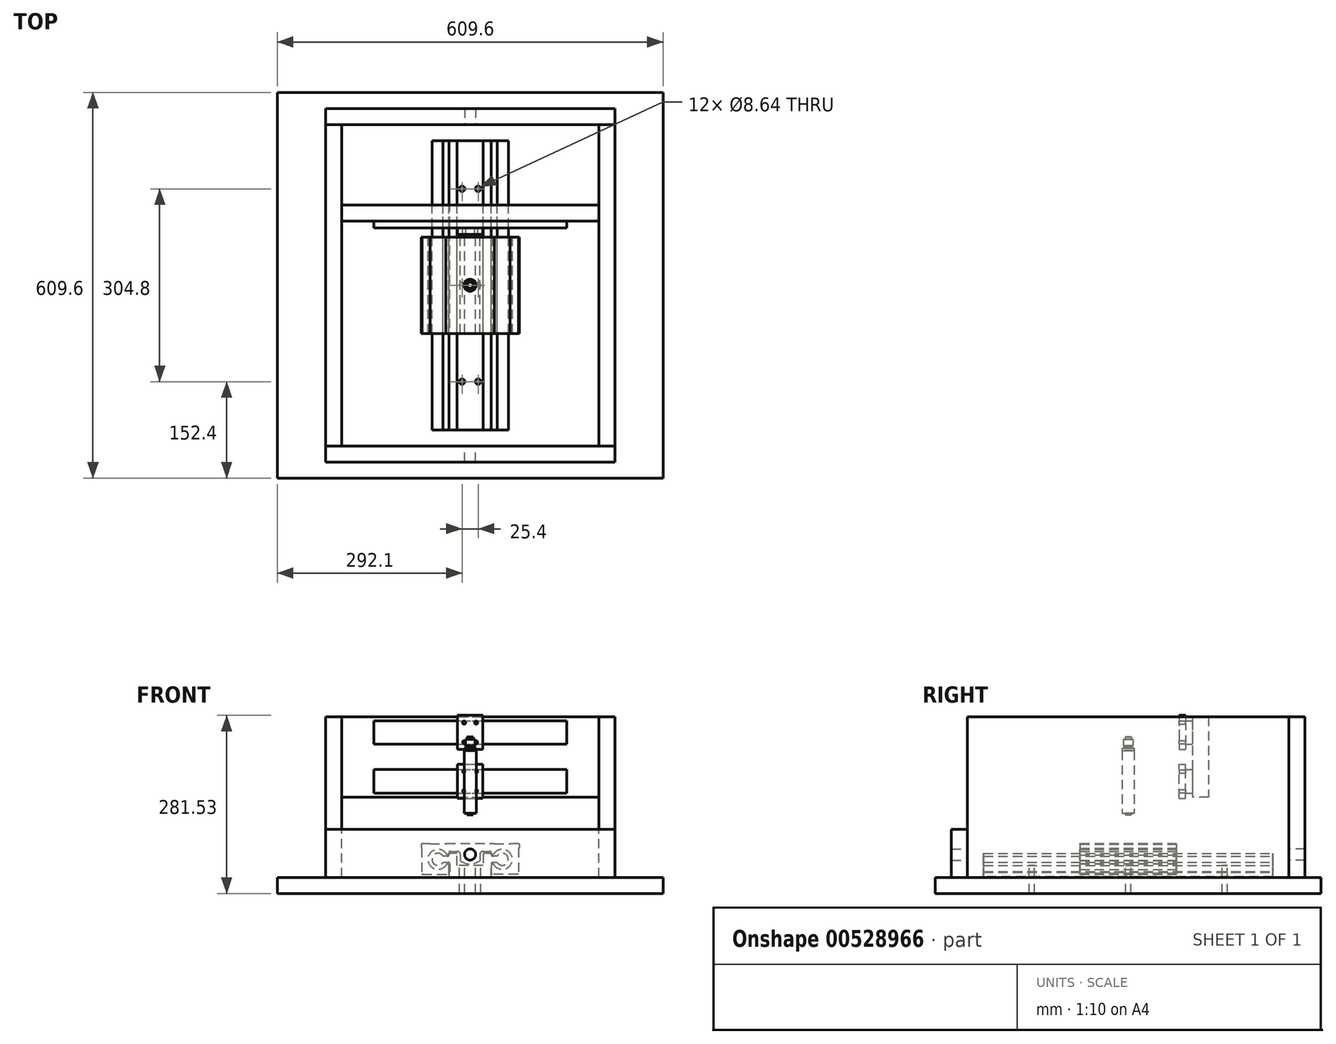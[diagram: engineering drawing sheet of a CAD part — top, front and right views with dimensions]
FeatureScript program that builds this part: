
annotation { "Feature Type Name" : "Feature", "Feature Type Description" : "" }
export const myFeature = defineFeature(function(context is Context, id is Id, definition is map)
    precondition{}
    {
        {
            var Q0;
            Q0=qCreatedBy(makeId("Front.planeOp"),FACE);
            var sketch = newSketch(context, id + "F0", { "sketchPlane" : qUnion([Q0])});
            skLineSegment(sketch, "E0", {"start": v(-33.4, 0) * mm, "end": v(33.4, 0) * mm});
            skLineSegment(sketch, "E1", {"start": v(33.4, 0) * mm, "end": v(33.4, 23.82) * mm});
            skLineSegment(sketch, "E2", {"start": v(33.4, 23.82) * mm, "end": v(42.47, 23.82) * mm});
            skLineSegment(sketch, "E3", {"start": v(42.47, 33.33) * mm, "end": v(33.4, 33.33) * mm});
            skLineSegment(sketch, "E4", {"start": v(33.4, 33.33) * mm, "end": v(33.4, 37.72) * mm});
            skLineSegment(sketch, "E5", {"start": v(33.4, 37.72) * mm, "end": v(20.57, 37.72) * mm});
            skLineSegment(sketch, "E6", {"start": v(20.57, 37.72) * mm, "end": v(20.57, 19.05) * mm});
            skLineSegment(sketch, "E7", {"start": v(20.57, 19.05) * mm, "end": v(-20.57, 19.05) * mm});
            skLineSegment(sketch, "E8", {"start": v(-20.57, 19.05) * mm, "end": v(-20.57, 37.72) * mm});
            skLineSegment(sketch, "E9", {"start": v(-20.57, 37.72) * mm, "end": v(-33.4, 37.72) * mm});
            skLineSegment(sketch, "E10", {"start": v(-33.4, 37.72) * mm, "end": v(-33.4, 33.33) * mm});
            skLineSegment(sketch, "E11", {"start": v(-33.4, 33.33) * mm, "end": v(-42.62, 33.33) * mm});
            skLineSegment(sketch, "E12", {"start": v(-42.62, 23.82) * mm, "end": v(-32.13, 23.82) * mm});
            skArc(sketch, "E13", {"start": v(-42.62, 33.33) * mm, "mid": v(-60.4, 28.57) * mm, "end": v(-42.62, 23.82) * mm});
            skLineSegment(sketch, "E14", {"start": v(0, 0) * mm, "end": v(0, 1053.14) * mm, "construction": true});
            skPoint(sketch, "E14.endSnap0", {"position": v(0, 19.05) * mm});
            skArc(sketch, "E15.MirrorC", {"start": v(42.47, 33.33) * mm, "mid": v(60.25, 28.58) * mm, "end": v(42.47, 23.82) * mm});
            skLineSegment(sketch, "E16", {"start": v(-33.4, 8.13) * mm, "end": v(-33.4, 0) * mm});
            skLineSegment(sketch, "E17", {"start": v(-32.13, 9.4) * mm, "end": v(-33.4, 8.13) * mm});
            skLineSegment(sketch, "E18", {"start": v(-32.13, 23.82) * mm, "end": v(-32.13, 9.4) * mm});
            skLineSegment(sketch, "E19", {"start": v(-42.62, 33.33) * mm, "end": v(-42.62, 23.82) * mm, "construction": true});
            skLineSegment(sketch, "E20", {"start": v(42.47, 33.33) * mm, "end": v(42.47, 23.82) * mm, "construction": true});
            skSolve(sketch);
        }
        {
            var Q0;
            Q0=makeQuery(id+"F0.imprint","IMPRINT",FACE,{"disambiguationData":[TD([[makeQuery(id+"F0.imprint","IMPRINT",EDGE,{"derivedFrom":sQuery(id+"F0.wireOp",EDGE,"E0")}),1.0]])]});
            extrude(context, id + "F1", {"entities" : qUnion([Q0]), "depth" : 228.6 * mm, "offsetDistance" : 25.4 * mm, "hasSecondDirection" : true, "secondDirectionOppositeDirection" : true, "secondDirectionDepth" : 228.6 * mm});
        }
        {
            var Q0;
            Q0=makeQuery(id+"F1.opExtrude","SWEPT_EDGE",EDGE,{"disambiguationData":[OSD([sQuery(id+"F0.wireOp",EDGE,"E0"),sQuery(id+"F0.wireOp",EDGE,"E16")])]});
            chamfer(context, id + "F2", {"entities" : qUnion([Q0]), "width" : 0.81 * mm, "tangentPropagation" : true});
        }
        {
            var Q0;
            Q0=makeQuery(id+"F1.opExtrude","SWEPT_EDGE",EDGE,{"disambiguationData":[OSD([sQuery(id+"F0.wireOp",EDGE,"E12"),sQuery(id+"F0.wireOp",EDGE,"E18")])]});
            var Q1;
            Q1=makeQuery(id+"F1.opExtrude","SWEPT_EDGE",EDGE,{"disambiguationData":[OSD([sQuery(id+"F0.wireOp",EDGE,"E10"),sQuery(id+"F0.wireOp",EDGE,"E11")])]});
            var Q2;
            Q2=makeQuery(id+"F1.opExtrude","SWEPT_EDGE",EDGE,{"disambiguationData":[OSD([sQuery(id+"F0.wireOp",EDGE,"E3"),sQuery(id+"F0.wireOp",EDGE,"E4")])]});
            var Q3;
            Q3=makeQuery(id+"F1.opExtrude","SWEPT_EDGE",EDGE,{"disambiguationData":[OSD([sQuery(id+"F0.wireOp",EDGE,"E1"),sQuery(id+"F0.wireOp",EDGE,"E2")])]});
            fillet(context, id + "F3", {"entities" : qUnion([Q0, Q1, Q2, Q3]), "radius" : 2.54 * mm, "tangentPropagation" : true, "allowEdgeOverflow" : false});
        }
        {
            var Q0;
            Q0=makeQuery(id+"F1.opExtrude","SWEPT_FACE",FACE,{"disambiguationData":[OSD([sQuery(id+"F0.wireOp",EDGE,"E7")])]});
            var sketch = newSketch(context, id + "F4", { "sketchPlane" : qUnion([Q0])});
            skCircle(sketch, "E21", {"center": v(-12.7, -152.4) * mm, "radius": 4.32 * mm});
            skCircle(sketch, "E22", {"center": v(12.7, -152.4) * mm, "radius": 4.32 * mm});
            skLineSegment(sketch, "E23", {"start": v(-12.7, -152.4) * mm, "end": v(12.7, -152.4) * mm, "construction": true});
            skLineSegment(sketch, "E24", {"start": v(0, 0) * mm, "end": v(0, -152.4) * mm, "construction": true});
            skCircle(sketch, "E25.0.1.0", {"center": v(-12.7, 0) * mm, "radius": 4.32 * mm});
            skCircle(sketch, "E25.0.1.1", {"center": v(12.7, 0) * mm, "radius": 4.32 * mm});
            skCircle(sketch, "E25.0.2.0", {"center": v(-12.7, 152.4) * mm, "radius": 4.32 * mm});
            skCircle(sketch, "E25.0.2.1", {"center": v(12.7, 152.4) * mm, "radius": 4.32 * mm});
            skLineSegment(sketch, "E25.direction2", {"start": v(-12.7, -152.4) * mm, "end": v(-12.7, 0) * mm, "construction": true});
            skSolve(sketch);
        }
        {
            var Q0;
            Q0=sQuery(id+"F4.wireOp",VERTEX,"E21.center");
            var Q1;
            Q1=sQuery(id+"F4.wireOp",VERTEX,"E22.center");
            var Q2;
            Q2=sQuery(id+"F4.wireOp",VERTEX,"E25.0.1.0.center");
            var Q3;
            Q3=sQuery(id+"F4.wireOp",VERTEX,"E25.0.1.1.center");
            var Q4;
            Q4=sQuery(id+"F4.wireOp",VERTEX,"E25.0.2.0.center");
            var Q5;
            Q5=sQuery(id+"F4.wireOp",VERTEX,"E25.0.2.1.center");
            var Q6;
            Q6=makeQuery(id+"F1.opExtrude","SWEPT_BODY",BODY,{"disambiguationData":[OSD([sQuery(id+"F0.wireOp",EDGE,"E0"),sQuery(id+"F0.wireOp",EDGE,"E1"),sQuery(id+"F0.wireOp",EDGE,"E2"),sQuery(id+"F0.wireOp",EDGE,"E3"),sQuery(id+"F0.wireOp",EDGE,"E4"),sQuery(id+"F0.wireOp",EDGE,"E5"),sQuery(id+"F0.wireOp",EDGE,"E6"),sQuery(id+"F0.wireOp",EDGE,"E7"),sQuery(id+"F0.wireOp",EDGE,"E8"),sQuery(id+"F0.wireOp",EDGE,"E9"),sQuery(id+"F0.wireOp",EDGE,"E10"),sQuery(id+"F0.wireOp",EDGE,"E11"),sQuery(id+"F0.wireOp",EDGE,"E12"),sQuery(id+"F0.wireOp",EDGE,"E13"),sQuery(id+"F0.wireOp",EDGE,"E15.MirrorC"),sQuery(id+"F0.wireOp",EDGE,"E16"),sQuery(id+"F0.wireOp",EDGE,"E17"),sQuery(id+"F0.wireOp",EDGE,"E18")])]});
            hole(context, id + "F5", {"style" : HoleStyle.SIMPLE, "endStyle" : HoleEndStyle.THROUGH, "holeDiameter" : 8.64 * mm, "isTappedThrough" : true, "tappedDepth" : 12.7 * mm, "tapClearance" : 3, "locations" : qUnion([Q0, Q1, Q2, Q3, Q4, Q5]), "scope" : qUnion([Q6])});
        }
        {
            var Q0;
            Q0=qCreatedBy(makeId("Front.planeOp"),FACE);
            var sketch = newSketch(context, id + "F6", { "sketchPlane" : qUnion([Q0])});
            skLineSegment(sketch, "E26.bottom", {"start": v(-77.55, 53.98) * mm, "end": v(-63.58, 53.98) * mm});
            skLineSegment(sketch, "E26.top", {"start": v(-76.78, 4.95) * mm, "end": v(-33.73, 4.95) * mm});
            skLineSegment(sketch, "E26.left", {"start": v(-77.55, 53.98) * mm, "end": v(-77.55, 46.35) * mm});
            skArc(sketch, "E27.0", {"start": v(-42.62, 33.33) * mm, "mid": v(-60.4, 28.57) * mm, "end": v(-42.62, 23.82) * mm, "construction": true});
            skArc(sketch, "E28", {"start": v(-36.33, 34.93) * mm, "mid": v(-66.75, 28.57) * mm, "end": v(-36.33, 22.23) * mm});
            skLineSegment(sketch, "E29.top", {"start": v(-63.58, 53.21) * mm, "end": v(-38.18, 53.21) * mm});
            skLineSegment(sketch, "E29.left", {"start": v(-63.58, 53.97) * mm, "end": v(-63.58, 53.21) * mm});
            skLineSegment(sketch, "E29.right", {"start": v(-38.18, 53.98) * mm, "end": v(-38.18, 53.21) * mm});
            skLineSegment(sketch, "E30.trimOffspring", {"start": v(-38.18, 53.98) * mm, "end": v(38.02, 53.98) * mm});
            skLineSegment(sketch, "E31", {"start": v(-50.88, 28.58) * mm, "end": v(-50.88, 53.21) * mm, "construction": true});
            skLineSegment(sketch, "E32.bottom", {"start": v(-77.55, 46.35) * mm, "end": v(-76.78, 46.35) * mm});
            skLineSegment(sketch, "E32.right", {"start": v(-76.78, 46.35) * mm, "end": v(-76.78, 4.95) * mm});
            skLineSegment(sketch, "E33", {"start": v(-33.73, 4.95) * mm, "end": v(-33.73, 19.63) * mm});
            skLineSegment(sketch, "E34", {"start": v(-33.73, 41.27) * mm, "end": v(-15.63, 41.27) * mm});
            skLineSegment(sketch, "E35", {"start": v(-33.73, 19.63) * mm, "end": v(-36.33, 22.23) * mm});
            skLineSegment(sketch, "E36", {"start": v(-36.33, 22.23) * mm, "end": v(-36.33, 34.93) * mm, "construction": true});
            skLineSegment(sketch, "E37", {"start": v(-36.33, 34.93) * mm, "end": v(-33.73, 37.52) * mm});
            skArc(sketch, "E38.0", {"start": v(42.47, 33.33) * mm, "mid": v(60.25, 28.58) * mm, "end": v(42.47, 23.82) * mm, "construction": true});
            skArc(sketch, "E39", {"start": v(36.17, 22.23) * mm, "mid": v(66.6, 28.58) * mm, "end": v(36.17, 34.93) * mm});
            skLineSegment(sketch, "E40.trimOffspring", {"start": v(-33.73, 37.52) * mm, "end": v(-33.73, 41.27) * mm});
            skLineSegment(sketch, "E41", {"start": v(-33.73, 37.52) * mm, "end": v(-33.73, 19.63) * mm, "construction": true});
            skLineSegment(sketch, "E42", {"start": v(-50.88, 28.58) * mm, "end": v(50.72, 28.58) * mm, "construction": true});
            skLineSegment(sketch, "E43", {"start": v(38.02, 53.98) * mm, "end": v(38.02, 53.21) * mm});
            skLineSegment(sketch, "E44", {"start": v(38.02, 53.21) * mm, "end": v(63.42, 53.21) * mm});
            skLineSegment(sketch, "E45", {"start": v(63.42, 53.21) * mm, "end": v(63.42, 53.98) * mm});
            skLineSegment(sketch, "E46", {"start": v(63.42, 53.98) * mm, "end": v(77.4, 53.98) * mm});
            skLineSegment(sketch, "E47", {"start": v(77.4, 53.98) * mm, "end": v(77.4, 46.35) * mm});
            skLineSegment(sketch, "E48", {"start": v(77.4, 46.35) * mm, "end": v(76.63, 46.35) * mm});
            skLineSegment(sketch, "E49", {"start": v(76.63, 46.35) * mm, "end": v(76.63, 4.95) * mm});
            skLineSegment(sketch, "E50", {"start": v(76.63, 4.95) * mm, "end": v(33.58, 4.95) * mm});
            skLineSegment(sketch, "E51", {"start": v(33.58, 4.95) * mm, "end": v(33.58, 19.63) * mm});
            skLineSegment(sketch, "E52", {"start": v(33.58, 19.63) * mm, "end": v(36.17, 22.23) * mm});
            skLineSegment(sketch, "E53", {"start": v(36.17, 22.23) * mm, "end": v(36.17, 34.93) * mm, "construction": true});
            skLineSegment(sketch, "E54", {"start": v(36.17, 34.93) * mm, "end": v(33.58, 37.52) * mm});
            skLineSegment(sketch, "E55", {"start": v(33.58, 37.52) * mm, "end": v(33.58, 41.27) * mm});
            skLineSegment(sketch, "E56", {"start": v(50.72, 28.58) * mm, "end": v(50.72, 53.21) * mm, "construction": true});
            skLineSegment(sketch, "E57", {"start": v(-0.08, 28.58) * mm, "end": v(-0.08, 53.98) * mm, "construction": true});
            skLineSegment(sketch, "E58", {"start": v(33.58, 37.52) * mm, "end": v(33.58, 19.63) * mm, "construction": true});
            skLineSegment(sketch, "E59", {"start": v(-33.73, 4.95) * mm, "end": v(33.58, 4.95) * mm, "construction": true});
            skArc(sketch, "E60", {"start": v(-15.63, 26.53) * mm, "mid": v(-0.08, 21.2) * mm, "end": v(15.48, 26.53) * mm});
            skLineSegment(sketch, "E61", {"start": v(-15.63, 41.27) * mm, "end": v(-15.63, 26.53) * mm});
            skLineSegment(sketch, "E62", {"start": v(15.48, 41.27) * mm, "end": v(15.48, 26.53) * mm});
            skLineSegment(sketch, "E63.trimOffspring", {"start": v(15.48, 41.27) * mm, "end": v(33.58, 41.27) * mm});
            skCircle(sketch, "E64", {"center": v(-0.08, 36.2) * mm, "radius": 8.9 * mm});
            skSolve(sketch);
        }
        {
            var Q0;
            Q0=makeQuery(id+"F6.imprint","IMPRINT",FACE,{"disambiguationData":[TD([[makeQuery(id+"F6.imprint","IMPRINT",EDGE,{"derivedFrom":sQuery(id+"F6.wireOp",EDGE,"E26.bottom")}),-1.0]])]});
            extrude(context, id + "F7", {"entities" : qUnion([Q0]), "depth" : 76.2 * mm, "offsetDistance" : 25.4 * mm, "hasSecondDirection" : true, "secondDirectionOppositeDirection" : true, "secondDirectionDepth" : 76.2 * mm});
        }
        {
            var Q0;
            Q0=makeQuery(id+"F7.opExtrude","SWEPT_EDGE",EDGE,{"disambiguationData":[OSD([sQuery(id+"F6.wireOp",EDGE,"E34"),sQuery(id+"F6.wireOp",EDGE,"E61")])]});
            var Q1;
            Q1=makeQuery(id+"F7.opExtrude","SWEPT_EDGE",EDGE,{"disambiguationData":[OSD([sQuery(id+"F6.wireOp",EDGE,"E62"),sQuery(id+"F6.wireOp",EDGE,"E63.trimOffspring")])]});
            fillet(context, id + "F8", {"entities" : qUnion([Q0, Q1]), "radius" : 5.08 * mm, "tangentPropagation" : true, "allowEdgeOverflow" : false});
        }
        {
            var Q0;
            Q0=makeQuery(id+"F7.opExtrude","SWEPT_EDGE",EDGE,{"disambiguationData":[OSD([sQuery(id+"F6.wireOp",EDGE,"E34"),sQuery(id+"F6.wireOp",EDGE,"E40.trimOffspring")])]});
            var Q1;
            Q1=makeQuery(id+"F7.opExtrude","SWEPT_EDGE",EDGE,{"disambiguationData":[OSD([sQuery(id+"F6.wireOp",EDGE,"E55"),sQuery(id+"F6.wireOp",EDGE,"E63.trimOffspring")])]});
            fillet(context, id + "F9", {"entities" : qUnion([Q0, Q1]), "radius" : 2.54 * mm, "tangentPropagation" : true, "allowEdgeOverflow" : false});
        }
        {
            var Q0;
            Q0=makeQuery(id+"F7.opExtrude","SWEPT_EDGE",EDGE,{"disambiguationData":[OSD([sQuery(id+"F6.wireOp",EDGE,"E28"),sQuery(id+"F6.wireOp",EDGE,"E37")])]});
            var Q1;
            Q1=makeQuery(id+"F7.opExtrude","SWEPT_EDGE",EDGE,{"disambiguationData":[OSD([sQuery(id+"F6.wireOp",EDGE,"E28"),sQuery(id+"F6.wireOp",EDGE,"E35")])]});
            var Q2;
            Q2=makeQuery(id+"F7.opExtrude","SWEPT_EDGE",EDGE,{"disambiguationData":[OSD([sQuery(id+"F6.wireOp",EDGE,"E39"),sQuery(id+"F6.wireOp",EDGE,"E54")])]});
            var Q3;
            Q3=makeQuery(id+"F7.opExtrude","SWEPT_EDGE",EDGE,{"disambiguationData":[OSD([sQuery(id+"F6.wireOp",EDGE,"E39"),sQuery(id+"F6.wireOp",EDGE,"E52")])]});
            var Q4;
            Q4=makeQuery(id+"F7.opExtrude","SWEPT_EDGE",EDGE,{"disambiguationData":[OSD([sQuery(id+"F6.wireOp",EDGE,"E37"),sQuery(id+"F6.wireOp",EDGE,"E40.trimOffspring")])]});
            var Q5;
            Q5=makeQuery(id+"F7.opExtrude","SWEPT_EDGE",EDGE,{"disambiguationData":[OSD([sQuery(id+"F6.wireOp",EDGE,"E33"),sQuery(id+"F6.wireOp",EDGE,"E35")])]});
            var Q6;
            Q6=makeQuery(id+"F7.opExtrude","SWEPT_EDGE",EDGE,{"disambiguationData":[OSD([sQuery(id+"F6.wireOp",EDGE,"E54"),sQuery(id+"F6.wireOp",EDGE,"E55")])]});
            var Q7;
            Q7=makeQuery(id+"F7.opExtrude","SWEPT_EDGE",EDGE,{"disambiguationData":[OSD([sQuery(id+"F6.wireOp",EDGE,"E51"),sQuery(id+"F6.wireOp",EDGE,"E52")])]});
            fillet(context, id + "F10", {"entities" : qUnion([Q0, Q1, Q2, Q3, Q4, Q5, Q6, Q7]), "radius" : 0.64 * mm, "tangentPropagation" : true, "allowEdgeOverflow" : false});
        }
        {
            var Q0;
            Q0=makeQuery(id+"F7.opExtrude","SWEPT_EDGE",EDGE,{"disambiguationData":[OSD([sQuery(id+"F6.wireOp",EDGE,"E26.top"),sQuery(id+"F6.wireOp",EDGE,"E32.right")])]});
            var Q1;
            Q1=makeQuery(id+"F7.opExtrude","SWEPT_EDGE",EDGE,{"disambiguationData":[OSD([sQuery(id+"F6.wireOp",EDGE,"E26.top"),sQuery(id+"F6.wireOp",EDGE,"E33")])]});
            var Q2;
            Q2=makeQuery(id+"F7.opExtrude","SWEPT_EDGE",EDGE,{"disambiguationData":[OSD([sQuery(id+"F6.wireOp",EDGE,"E50"),sQuery(id+"F6.wireOp",EDGE,"E51")])]});
            var Q3;
            Q3=makeQuery(id+"F7.opExtrude","SWEPT_EDGE",EDGE,{"disambiguationData":[OSD([sQuery(id+"F6.wireOp",EDGE,"E49"),sQuery(id+"F6.wireOp",EDGE,"E50")])]});
            var Q4;
            Q4=makeQuery(id+"F7.opExtrude","SWEPT_EDGE",EDGE,{"disambiguationData":[OSD([sQuery(id+"F6.wireOp",EDGE,"E26.bottom"),sQuery(id+"F6.wireOp",EDGE,"E26.left")])]});
            var Q5;
            Q5=makeQuery(id+"F7.opExtrude","SWEPT_EDGE",EDGE,{"disambiguationData":[OSD([sQuery(id+"F6.wireOp",EDGE,"E46"),sQuery(id+"F6.wireOp",EDGE,"E47")])]});
            chamfer(context, id + "F11", {"entities" : qUnion([Q0, Q1, Q2, Q3, Q4, Q5]), "width" : 1.27 * mm, "tangentPropagation" : true});
        }
        {
            var Q0;
            Q0=qCreatedBy(makeId("Top.planeOp"),FACE);
            var sketch = newSketch(context, id + "F12", { "sketchPlane" : qUnion([Q0])});
            skLineSegment(sketch, "E65.bottom", {"start": v(304.8, 304.8) * mm, "end": v(-304.8, 304.8) * mm});
            skLineSegment(sketch, "E65.top", {"start": v(304.8, -304.8) * mm, "end": v(-304.8, -304.8) * mm});
            skLineSegment(sketch, "E65.left", {"start": v(304.8, 304.8) * mm, "end": v(304.8, -304.8) * mm});
            skLineSegment(sketch, "E65.right", {"start": v(-304.8, 304.8) * mm, "end": v(-304.8, -304.8) * mm});
            skPoint(sketch, "E65.middle", {"position": v(0, 0) * mm});
            skCircle(sketch, "E66", {"center": v(-12.7, -152.4) * mm, "radius": 4.32 * mm});
            skCircle(sketch, "E67.0.1.0", {"center": v(-12.7, 0) * mm, "radius": 4.32 * mm});
            skCircle(sketch, "E67.0.2.0", {"center": v(-12.7, 152.4) * mm, "radius": 4.32 * mm});
            skCircle(sketch, "E67.1.0.0", {"center": v(12.7, -152.4) * mm, "radius": 4.32 * mm});
            skCircle(sketch, "E67.1.1.0", {"center": v(12.7, 0) * mm, "radius": 4.32 * mm});
            skCircle(sketch, "E67.1.2.0", {"center": v(12.7, 152.4) * mm, "radius": 4.32 * mm});
            skLineSegment(sketch, "E67.direction1", {"start": v(-12.7, -152.4) * mm, "end": v(12.7, -152.4) * mm, "construction": true});
            skLineSegment(sketch, "E67.direction2", {"start": v(-12.7, -152.4) * mm, "end": v(-12.7, 0) * mm, "construction": true});
            skLineSegment(sketch, "E68", {"start": v(12.7, 0) * mm, "end": v(-12.7, 0) * mm, "construction": true});
            skSolve(sketch);
        }
        {
            var Q0;
            Q0=makeQuery(id+"F12.imprint","IMPRINT",FACE,{"disambiguationData":[TD([[makeQuery(id+"F12.imprint","IMPRINT",EDGE,{"derivedFrom":sQuery(id+"F12.wireOp",EDGE,"E65.bottom")}),1.0]])]});
            extrude(context, id + "F13", {"entities" : qUnion([Q0]), "oppositeDirection" : true, "depth" : 25.4 * mm, "offsetDistance" : 25.4 * mm});
        }
        {
            var Q0;
            Q0=qCreatedBy(makeId("Right.planeOp"),FACE);
            cPlane(context, id + "F14", {"entities" : qUnion([Q0]), "cplaneType" : CPlaneType.OFFSET, "offset" : 203.2 * mm, "width" : 152.4 * mm, "height" : 152.4 * mm});
        }
        {
            var Q0;
            Q0=qCreatedBy(id+"F14.planeOp",FACE);
            var sketch = newSketch(context, id + "F15", { "sketchPlane" : qUnion([Q0])});
            skLineSegment(sketch, "E69.bottom", {"start": v(-254, 0) * mm, "end": v(254, 0) * mm});
            skLineSegment(sketch, "E69.top", {"start": v(-254, 254) * mm, "end": v(254, 254) * mm});
            skLineSegment(sketch, "E69.left", {"start": v(-254, 0) * mm, "end": v(-254, 254) * mm});
            skLineSegment(sketch, "E69.right", {"start": v(254, 0) * mm, "end": v(254, 254) * mm});
            skSolve(sketch);
        }
        {
            var Q0;
            Q0=makeQuery(id+"F15.imprint","IMPRINT",FACE,{"disambiguationData":[TD([[makeQuery(id+"F15.imprint","IMPRINT",EDGE,{"derivedFrom":sQuery(id+"F15.wireOp",EDGE,"E69.bottom")}),1.0]])]});
            extrude(context, id + "F16", {"entities" : qUnion([Q0]), "depth" : 25.4 * mm, "offsetDistance" : 25.4 * mm});
        }
        {
            var Q0;
            Q0=makeQuery(id+"F16.opExtrude","SWEPT_BODY",BODY,{"disambiguationData":[OSD([sQuery(id+"F15.wireOp",EDGE,"E69.bottom"),sQuery(id+"F15.wireOp",EDGE,"E69.top"),sQuery(id+"F15.wireOp",EDGE,"E69.left"),sQuery(id+"F15.wireOp",EDGE,"E69.right")])]});
            var Q1;
            Q1=qCreatedBy(makeId("Right.planeOp"),FACE);
            mirror(context, id + "F17", {"entities" : qUnion([Q0]), "mirrorPlane" : qUnion([Q1])});
        }
        {
            var Q0;
            Q0=makeQuery(id+"F17.opPattern","COPY",FACE,{"derivedFrom":makeQuery(id+"F16.opExtrude","SWEPT_FACE",FACE,{"disambiguationData":[OSD([sQuery(id+"F15.wireOp",EDGE,"E69.left")])]}),"instanceName":"1"});
            var sketch = newSketch(context, id + "F18", { "sketchPlane" : qUnion([Q0])});
            skLineSegment(sketch, "E70.bottom", {"start": v(-228.6, 0) * mm, "end": v(228.6, 0) * mm});
            skLineSegment(sketch, "E70.top", {"start": v(-228.6, 76.2) * mm, "end": v(228.6, 76.2) * mm});
            skLineSegment(sketch, "E70.left", {"start": v(-228.6, 0) * mm, "end": v(-228.6, 76.2) * mm});
            skLineSegment(sketch, "E70.right", {"start": v(228.6, 0) * mm, "end": v(228.6, 76.2) * mm});
            skCircle(sketch, "E71.0", {"center": v(-0.08, 36.2) * mm, "radius": 8.9 * mm});
            skSolve(sketch);
        }
        {
            var Q0;
            {var subQ4=sQuery(id+"F18.wireOp",EDGE,"E70.left");Q0=makeQuery(id+"F18.imprint","IMPRINT",FACE,{"disambiguationData":[TD([[makeQuery(id+"F18.imprint","IMPRINT",EDGE,{"derivedFrom":subQ4}),-1.0]])]});}
            var Q1;
            {var subQ3=sQuery(id+"F18.wireOp",EDGE,"E70.right");Q1=makeQuery(id+"F18.imprint","IMPRINT",FACE,{"disambiguationData":[TD([[makeQuery(id+"F18.imprint","IMPRINT",EDGE,{"derivedFrom":subQ3}),1.0]])]});}
            extrude(context, id + "F19", {"entities" : qUnion([Q0, Q1]), "depth" : 25.4 * mm, "offsetDistance" : 25.4 * mm});
        }
        {
            var Q0;
            Q0=makeQuery(id+"F16.opExtrude","SWEPT_FACE",FACE,{"disambiguationData":[OSD([sQuery(id+"F15.wireOp",EDGE,"E69.right")])]});
            var sketch = newSketch(context, id + "F20", { "sketchPlane" : qUnion([Q0])});
            skLineSegment(sketch, "E72.bottom", {"start": v(-228.6, 0) * mm, "end": v(228.6, 0) * mm});
            skLineSegment(sketch, "E72.top", {"start": v(-228.6, 254) * mm, "end": v(228.6, 254) * mm});
            skLineSegment(sketch, "E72.left", {"start": v(-228.6, 0) * mm, "end": v(-228.6, 254) * mm});
            skLineSegment(sketch, "E72.right", {"start": v(228.6, 0) * mm, "end": v(228.6, 254) * mm});
            skCircle(sketch, "E73.0", {"center": v(0.08, 36.2) * mm, "radius": 8.9 * mm});
            skSolve(sketch);
        }
        {
            var Q0;
            {var subQ2=sQuery(id+"F20.wireOp",EDGE,"E72.left");Q0=makeQuery(id+"F20.imprint","IMPRINT",FACE,{"disambiguationData":[TD([[makeQuery(id+"F20.imprint","IMPRINT",EDGE,{"derivedFrom":subQ2}),-1.0]])]});}
            var Q1;
            Q1=makeQuery(id+"F20.imprint","IMPRINT",FACE,{"disambiguationData":[TD([[makeQuery(id+"F20.imprint","IMPRINT",EDGE,{"derivedFrom":sQuery(id+"F20.wireOp",EDGE,"E73.0")}),-1.0]])]});
            extrude(context, id + "F21", {"entities" : qUnion([Q0, Q1]), "depth" : 25.4 * mm, "offsetDistance" : 25.4 * mm});
        }
        {
            var Q0;
            Q0=qCreatedBy(makeId("Front.planeOp"),FACE);
            var sketch = newSketch(context, id + "F22", { "sketchPlane" : qUnion([Q0])});
            skLineSegment(sketch, "E74", {"start": v(0, 0) * mm, "end": v(0, 101.6) * mm, "construction": true});
            skLineSegment(sketch, "E75.bottom", {"start": v(9.52, 101.6) * mm, "end": v(-9.53, 101.6) * mm});
            skLineSegment(sketch, "E75.top", {"start": v(9.52, 200.15) * mm, "end": v(-9.53, 200.15) * mm});
            skLineSegment(sketch, "E75.left", {"start": v(9.52, 101.6) * mm, "end": v(9.52, 200.15) * mm});
            skLineSegment(sketch, "E75.right", {"start": v(-9.53, 101.6) * mm, "end": v(-9.53, 200.15) * mm});
            skPoint(sketch, "E75.middle", {"position": v(0, 150.88) * mm});
            skLineSegment(sketch, "E76.bottom", {"start": v(4.76, 99.06) * mm, "end": v(-4.76, 99.06) * mm});
            skLineSegment(sketch, "E76.top", {"start": v(4.76, 101.6) * mm, "end": v(-4.76, 101.6) * mm});
            skLineSegment(sketch, "E76.left", {"start": v(4.76, 99.06) * mm, "end": v(4.76, 101.6) * mm});
            skLineSegment(sketch, "E76.right", {"start": v(-4.76, 99.06) * mm, "end": v(-4.76, 101.6) * mm});
            skPoint(sketch, "E76.middle", {"position": v(0, 100.33) * mm});
            skLineSegment(sketch, "E77.bottom", {"start": v(9.52, 204.34) * mm, "end": v(-9.53, 204.34) * mm});
            skLineSegment(sketch, "E77.top", {"start": v(9.52, 200.66) * mm, "end": v(-9.53, 200.66) * mm});
            skLineSegment(sketch, "E77.left", {"start": v(9.52, 204.34) * mm, "end": v(9.52, 200.66) * mm});
            skLineSegment(sketch, "E77.right", {"start": v(-9.53, 204.34) * mm, "end": v(-9.53, 200.66) * mm});
            skPoint(sketch, "E77.middle", {"position": v(0, 202.5) * mm});
            skLineSegment(sketch, "E78.bottom", {"start": v(7.6, 205.61) * mm, "end": v(-7.6, 205.61) * mm});
            skLineSegment(sketch, "E78.top", {"start": v(7.6, 204.34) * mm, "end": v(-7.6, 204.34) * mm});
            skLineSegment(sketch, "E78.left", {"start": v(7.6, 205.61) * mm, "end": v(7.6, 204.34) * mm});
            skLineSegment(sketch, "E78.right", {"start": v(-7.6, 205.61) * mm, "end": v(-7.6, 204.34) * mm});
            skPoint(sketch, "E78.middle", {"position": v(0, 204.98) * mm});
            skLineSegment(sketch, "E79.bottom", {"start": v(7.6, 217.98) * mm, "end": v(-7.6, 217.98) * mm});
            skLineSegment(sketch, "E79.top", {"start": v(7.6, 208.2) * mm, "end": v(-7.6, 208.2) * mm});
            skLineSegment(sketch, "E79.left", {"start": v(7.6, 217.98) * mm, "end": v(7.6, 208.2) * mm});
            skLineSegment(sketch, "E79.right", {"start": v(-7.6, 217.98) * mm, "end": v(-7.6, 208.2) * mm});
            skPoint(sketch, "E79.middle", {"position": v(0, 213.1) * mm});
            skLineSegment(sketch, "E80.bottom", {"start": v(4.76, 222.05) * mm, "end": v(-4.76, 222.05) * mm});
            skLineSegment(sketch, "E80.top", {"start": v(4.76, 217.98) * mm, "end": v(-4.76, 217.98) * mm});
            skLineSegment(sketch, "E80.left", {"start": v(4.76, 222.05) * mm, "end": v(4.76, 217.98) * mm});
            skLineSegment(sketch, "E80.right", {"start": v(-4.76, 222.05) * mm, "end": v(-4.76, 217.98) * mm});
            skPoint(sketch, "E80.middle", {"position": v(0, 220.01) * mm});
            skLineSegment(sketch, "E81.bottom", {"start": v(8.89, 200.66) * mm, "end": v(-8.9, 200.66) * mm});
            skLineSegment(sketch, "E81.top", {"start": v(8.89, 200.15) * mm, "end": v(-8.9, 200.15) * mm});
            skLineSegment(sketch, "E81.left", {"start": v(8.89, 200.66) * mm, "end": v(8.89, 200.15) * mm});
            skLineSegment(sketch, "E81.right", {"start": v(-8.9, 200.66) * mm, "end": v(-8.9, 200.15) * mm});
            skPoint(sketch, "E81.middle", {"position": v(0, 200.4) * mm});
            skLineSegment(sketch, "E82", {"start": v(-7.6, 205.61) * mm, "end": v(-7.6, 208.2) * mm, "construction": true});
            skLineSegment(sketch, "E83", {"start": v(7.6, 208.2) * mm, "end": v(7.6, 205.61) * mm, "construction": true});
            skArc(sketch, "E84", {"start": v(7.6, 208.2) * mm, "mid": v(6.3, 206.9) * mm, "end": v(7.6, 205.61) * mm});
            skArc(sketch, "E85", {"start": v(-7.6, 205.61) * mm, "mid": v(-6.3, 206.9) * mm, "end": v(-7.6, 208.2) * mm});
            skLineSegment(sketch, "E86", {"start": v(0, 99.06) * mm, "end": v(0, 222.05) * mm});
            skSolve(sketch);
        }
        {
            var Q0;
            {var subQ0=sQuery(id+"F22.wireOp",EDGE,"E76.left");Q0=makeQuery(id+"F22.imprint","IMPRINT",FACE,{"disambiguationData":[TD([[makeQuery(id+"F22.imprint","IMPRINT",EDGE,{"derivedFrom":subQ0}),1.0]])]});}
            var Q1;
            {var subQ5=sQuery(id+"F22.wireOp",EDGE,"E75.left");Q1=makeQuery(id+"F22.imprint","IMPRINT",FACE,{"disambiguationData":[TD([[makeQuery(id+"F22.imprint","IMPRINT",EDGE,{"derivedFrom":subQ5}),1.0]])]});}
            var Q2;
            {var subQ0=sQuery(id+"F22.wireOp",EDGE,"E81.left");Q2=makeQuery(id+"F22.imprint","IMPRINT",FACE,{"disambiguationData":[TD([[makeQuery(id+"F22.imprint","IMPRINT",EDGE,{"derivedFrom":subQ0}),-1.0]])]});}
            var Q3;
            {var subQ5=sQuery(id+"F22.wireOp",EDGE,"E77.left");Q3=makeQuery(id+"F22.imprint","IMPRINT",FACE,{"disambiguationData":[TD([[makeQuery(id+"F22.imprint","IMPRINT",EDGE,{"derivedFrom":subQ5}),-1.0]])]});}
            var Q4;
            {var subQ0=sQuery(id+"F22.wireOp",EDGE,"E78.left");Q4=makeQuery(id+"F22.imprint","IMPRINT",FACE,{"disambiguationData":[TD([[makeQuery(id+"F22.imprint","IMPRINT",EDGE,{"derivedFrom":subQ0}),-1.0]])]});}
            var Q5;
            {var subQ0=sQuery(id+"F22.wireOp",EDGE,"E84");Q5=makeQuery(id+"F22.imprint","IMPRINT",FACE,{"disambiguationData":[TD([[makeQuery(id+"F22.imprint","IMPRINT",EDGE,{"derivedFrom":subQ0}),-1.0]])]});}
            var Q6;
            {var subQ5=sQuery(id+"F22.wireOp",EDGE,"E79.left");Q6=makeQuery(id+"F22.imprint","IMPRINT",FACE,{"disambiguationData":[TD([[makeQuery(id+"F22.imprint","IMPRINT",EDGE,{"derivedFrom":subQ5}),-1.0]])]});}
            var Q7;
            {var subQ0=sQuery(id+"F22.wireOp",EDGE,"E80.left");Q7=makeQuery(id+"F22.imprint","IMPRINT",FACE,{"disambiguationData":[TD([[makeQuery(id+"F22.imprint","IMPRINT",EDGE,{"derivedFrom":subQ0}),-1.0]])]});}
            var Q8;
            Q8=sQuery(id+"F22.wireOp",EDGE,"E86");
            revolve(context, id + "F23", {"entities" : qUnion([Q0, Q1, Q2, Q3, Q4, Q5, Q6, Q7]), "axis" : qUnion([Q8]), "revolveType" : RevolveType.FULL});
        }
        {
            var Q0;
            Q0=makeQuery(id+"F21.opExtrude","CAP_FACE",FACE,{"disambiguationData":[OSD([sQuery(id+"F20.wireOp",EDGE,"E72.bottom"),sQuery(id+"F20.wireOp",EDGE,"E72.top"),sQuery(id+"F20.wireOp",EDGE,"E72.left"),sQuery(id+"F20.wireOp",EDGE,"E72.right"),sQuery(id+"F20.wireOp",EDGE,"E73.0")])],"isStart":true});
            cPlane(context, id + "F24", {"entities" : qUnion([Q0]), "cplaneType" : CPlaneType.OFFSET, "offset" : 152.4 * mm, "width" : 152.4 * mm, "height" : 152.4 * mm});
        }
        {
            var Q0;
            Q0=qCreatedBy(id+"F24.planeOp",FACE);
            var sketch = newSketch(context, id + "F25", { "sketchPlane" : qUnion([Q0])});
            skLineSegment(sketch, "E87.0.1", {"start": v(-203.2, 254) * mm, "end": v(-203.2, 0) * mm});
            skLineSegment(sketch, "E87.0.3", {"start": v(-203.2, 0) * mm, "end": v(-203.2, 254) * mm});
            skLineSegment(sketch, "E88.0.1", {"start": v(203.2, 254) * mm, "end": v(203.2, 0) * mm});
            skLineSegment(sketch, "E88.0.3", {"start": v(203.2, 0) * mm, "end": v(203.2, 254) * mm});
            skLineSegment(sketch, "E89.bottom", {"start": v(-203.2, 254) * mm, "end": v(203.2, 254) * mm});
            skLineSegment(sketch, "E89.top", {"start": v(-203.2, 127) * mm, "end": v(203.2, 127) * mm});
            skLineSegment(sketch, "E89.left", {"start": v(-203.2, 254) * mm, "end": v(-203.2, 127) * mm});
            skLineSegment(sketch, "E89.right", {"start": v(203.2, 254) * mm, "end": v(203.2, 127) * mm});
            skLineSegment(sketch, "E90.bottom", {"start": v(-152.4, 247.65) * mm, "end": v(152.4, 247.65) * mm});
            skLineSegment(sketch, "E90.top", {"start": v(-152.4, 210.62) * mm, "end": v(152.4, 210.62) * mm});
            skLineSegment(sketch, "E90.left", {"start": v(-152.4, 247.65) * mm, "end": v(-152.4, 210.62) * mm});
            skLineSegment(sketch, "E90.right", {"start": v(152.4, 247.65) * mm, "end": v(152.4, 210.62) * mm});
            skLineSegment(sketch, "E91.bottom", {"start": v(-152.4, 170.38) * mm, "end": v(152.4, 170.38) * mm});
            skLineSegment(sketch, "E91.top", {"start": v(-152.4, 133.35) * mm, "end": v(152.4, 133.35) * mm});
            skLineSegment(sketch, "E91.left", {"start": v(-152.4, 170.38) * mm, "end": v(-152.4, 133.35) * mm});
            skLineSegment(sketch, "E91.right", {"start": v(152.4, 170.38) * mm, "end": v(152.4, 133.35) * mm});
            skLineSegment(sketch, "E92", {"start": v(0, 254) * mm, "end": v(0, 127) * mm, "construction": true});
            skSolve(sketch);
        }
        {
            var Q0;
            Q0=makeQuery(id+"F25.imprint","IMPRINT",FACE,{"disambiguationData":[TD([[makeQuery(id+"F25.imprint","IMPRINT",EDGE,{"derivedFrom":sQuery(id+"F25.wireOp",EDGE,"E89.bottom")}),-1.0]])]});
            var Q1;
            Q1=makeQuery(id+"F25.imprint","IMPRINT",FACE,{"disambiguationData":[TD([[makeQuery(id+"F25.imprint","IMPRINT",EDGE,{"derivedFrom":sQuery(id+"F25.wireOp",EDGE,"E90.bottom")}),-1.0]])]});
            var Q2;
            {var subQ0=sQuery(id+"F25.wireOp",EDGE,"E90.top");Q2=makeQuery(id+"F25.imprint","IMPRINT",FACE,{"disambiguationData":[TD([[makeQuery(id+"F25.imprint","IMPRINT",EDGE,{"derivedFrom":subQ0}),-1.0]])]});}
            var Q3;
            Q3=makeQuery(id+"F25.imprint","IMPRINT",FACE,{"disambiguationData":[TD([[makeQuery(id+"F25.imprint","IMPRINT",EDGE,{"derivedFrom":sQuery(id+"F25.wireOp",EDGE,"E91.bottom")}),-1.0]])]});
            var Q4;
            {var subQ0=sQuery(id+"F25.wireOp",EDGE,"E89.top");Q4=makeQuery(id+"F25.imprint","IMPRINT",FACE,{"disambiguationData":[TD([[makeQuery(id+"F25.imprint","IMPRINT",EDGE,{"derivedFrom":subQ0}),1.0]])]});}
            extrude(context, id + "F26", {"entities" : qUnion([Q0, Q1, Q2, Q3, Q4]), "oppositeDirection" : true, "depth" : 25.4 * mm, "offsetDistance" : 25.4 * mm});
        }
        {
            var Q0;
            Q0=makeQuery(id+"F25.imprint","IMPRINT",FACE,{"disambiguationData":[TD([[makeQuery(id+"F25.imprint","IMPRINT",EDGE,{"derivedFrom":sQuery(id+"F25.wireOp",EDGE,"E90.bottom")}),-1.0]])]});
            var Q1;
            Q1=makeQuery(id+"F25.imprint","IMPRINT",FACE,{"disambiguationData":[TD([[makeQuery(id+"F25.imprint","IMPRINT",EDGE,{"derivedFrom":sQuery(id+"F25.wireOp",EDGE,"E91.bottom")}),-1.0]])]});
            extrude(context, id + "F27", {"entities" : qUnion([Q0, Q1]), "operationType" : NewBodyOperationType.ADD, "depth" : 10.97 * mm, "offsetDistance" : 25.4 * mm});
        }
        {
            var Q0;
            Q0=makeQuery(id+"F27.opExtrude","CAP_FACE",FACE,{"disambiguationData":[OSD([sQuery(id+"F25.wireOp",EDGE,"E90.bottom"),sQuery(id+"F25.wireOp",EDGE,"E90.top"),sQuery(id+"F25.wireOp",EDGE,"E90.left"),sQuery(id+"F25.wireOp",EDGE,"E90.right")])],"isStart":false});
            var sketch = newSketch(context, id + "F28", { "sketchPlane" : qUnion([Q0])});
            skLineSegment(sketch, "E93.bottom", {"start": v(-20, 256.13) * mm, "end": v(20, 256.13) * mm});
            skLineSegment(sketch, "E93.top", {"start": v(-20, 202.13) * mm, "end": v(20, 202.13) * mm});
            skLineSegment(sketch, "E93.left", {"start": v(-20, 256.13) * mm, "end": v(-20, 202.13) * mm});
            skLineSegment(sketch, "E93.right", {"start": v(20, 256.13) * mm, "end": v(20, 202.13) * mm});
            skLineSegment(sketch, "E94", {"start": v(0, 256.13) * mm, "end": v(0, 202.13) * mm, "construction": true});
            skLineSegment(sketch, "E95", {"start": v(0, 247.65) * mm, "end": v(0, 210.62) * mm, "construction": true});
            skLineSegment(sketch, "E96", {"start": v(-152.4, 229.13) * mm, "end": v(152.4, 229.13) * mm, "construction": true});
            skPoint(sketch, "E97", {"position": v(0, 229.13) * mm});
            skLineSegment(sketch, "E98.0", {"start": v(-152.4, 170.38) * mm, "end": v(152.4, 170.38) * mm, "construction": true});
            skLineSegment(sketch, "E99", {"start": v(-152.4, 210.62) * mm, "end": v(-152.4, 170.38) * mm, "construction": true});
            skLineSegment(sketch, "E100", {"start": v(152.4, 210.62) * mm, "end": v(152.4, 170.38) * mm, "construction": true});
            skLineSegment(sketch, "E101", {"start": v(152.4, 190.5) * mm, "end": v(-152.4, 190.5) * mm, "construction": true});
            skLineSegment(sketch, "E102.bottom", {"start": v(9.5, 244.63) * mm, "end": v(-9.5, 244.63) * mm, "construction": true});
            skLineSegment(sketch, "E102.top", {"start": v(9.5, 213.63) * mm, "end": v(-9.5, 213.63) * mm, "construction": true});
            skLineSegment(sketch, "E102.left", {"start": v(9.5, 244.63) * mm, "end": v(9.5, 213.63) * mm, "construction": true});
            skLineSegment(sketch, "E102.right", {"start": v(-9.5, 244.63) * mm, "end": v(-9.5, 213.63) * mm, "construction": true});
            skCircle(sketch, "E103", {"center": v(-9.5, 244.63) * mm, "radius": 2.5 * mm});
            skCircle(sketch, "E104", {"center": v(9.5, 244.63) * mm, "radius": 2.5 * mm});
            skCircle(sketch, "E105", {"center": v(9.5, 213.63) * mm, "radius": 2.5 * mm});
            skCircle(sketch, "E106", {"center": v(-9.5, 213.63) * mm, "radius": 2.5 * mm});
            skSolve(sketch);
        }
        {
            var Q0;
            {var subQ0=sQuery(id+"F28.wireOp",EDGE,"E93.bottom");Q0=makeQuery(id+"F28.imprint","IMPRINT",FACE,{"disambiguationData":[TD([[makeQuery(id+"F28.imprint","IMPRINT",EDGE,{"derivedFrom":subQ0}),-1.0]])]});}
            var Q1;
            Q1=makeQuery(id+"F28.imprint","IMPRINT",FACE,{"disambiguationData":[TD([[makeQuery(id+"F28.imprint","IMPRINT",EDGE,{"derivedFrom":sQuery(id+"F28.wireOp",EDGE,"E103")}),-1.0]])]});
            var Q2;
            {var subQ0=sQuery(id+"F28.wireOp",EDGE,"E93.top");Q2=makeQuery(id+"F28.imprint","IMPRINT",FACE,{"disambiguationData":[TD([[makeQuery(id+"F28.imprint","IMPRINT",EDGE,{"derivedFrom":subQ0}),1.0]])]});}
            extrude(context, id + "F29", {"entities" : qUnion([Q0, Q1, Q2]), "depth" : 10 * mm, "offsetDistance" : 25.4 * mm});
        }
        {
            var Q0;
            Q0=makeQuery(id+"F27.opExtrude","SWEPT_FACE",FACE,{"disambiguationData":[OSD([sQuery(id+"F25.wireOp",EDGE,"E90.top")])]});
            var Q1;
            Q1=makeQuery(id+"F27.opExtrude","SWEPT_FACE",FACE,{"disambiguationData":[OSD([sQuery(id+"F25.wireOp",EDGE,"E91.bottom")])]});
            cPlane(context, id + "F30", {"entities" : qUnion([Q0, Q1]), "cplaneType" : CPlaneType.MID_PLANE, "offset" : 25.4 * mm, "width" : 152.4 * mm, "height" : 152.4 * mm});
        }
        {
            var Q0;
            Q0=makeQuery(id+"F29.opExtrude","SWEPT_BODY",BODY,{"disambiguationData":[OSD([sQuery(id+"F28.wireOp",EDGE,"E93.bottom"),sQuery(id+"F28.wireOp",EDGE,"E93.top"),sQuery(id+"F28.wireOp",EDGE,"E93.left"),sQuery(id+"F28.wireOp",EDGE,"E93.right"),sQuery(id+"F28.wireOp",EDGE,"E103"),sQuery(id+"F28.wireOp",EDGE,"E104"),sQuery(id+"F28.wireOp",EDGE,"E105"),sQuery(id+"F28.wireOp",EDGE,"E106")])]});
            var Q1;
            Q1=qCreatedBy(id+"F30.planeOp",FACE);
            mirror(context, id + "F31", {"operationType" : NewBodyOperationType.ADD, "entities" : qUnion([Q0]), "mirrorPlane" : qUnion([Q1])});
        }
    });
